# Revit family: Niche_NobleCompany_301_314
name_source: partatom
category: Generic Models
revit_build: Autodesk Revit 2016 (Build: 20150714_1515(x64)
units: mm (PartAtom-declared; Revit-internal decimal feet)

## family parameters
Always vertical = Yes
Can host rebar = No
Cut with Voids When Loaded = No
Host = Wall
Part Type = Normal
Room Calculation Point = No
Round Connector Dimension = Use Diameter
Shared = No

## types (2) — shared parameters
Assembly Code = D2010700
Depth = 0' - 4"
Installation-Fabrication = http://noblecompany.com
Keynote = 10 28 00
Manufacturer = Noble Company
Manufacturer Fax = 231-799-8850
Manufacturer Website = www.noblecompany.com
Niche Material = Acrylic Polymer Finish
Product Data = http://www.arcat.com
Product Properties = http://noblecompany.com
Revision = R1_09-2016
Sales Information = http://noblecompany.com
URL = www.noblecompany.com
Width = 1' - 2 1/4"

## per-type parameters (varying)
| type | Description | Height | Model | Thickness |
| 301 Square | 301 Square Niche | 1' - 2 1/4" | 301 | 0' - 1 1/8" |
| 314 Rectangular | 314 Rectangular NIche | 1' - 10 1/2" | 314 | 0' - 1 1/4" |

## geometry (parser evidence)
native form markers: Sweep x4
no freeform markers — native parametric forms only
